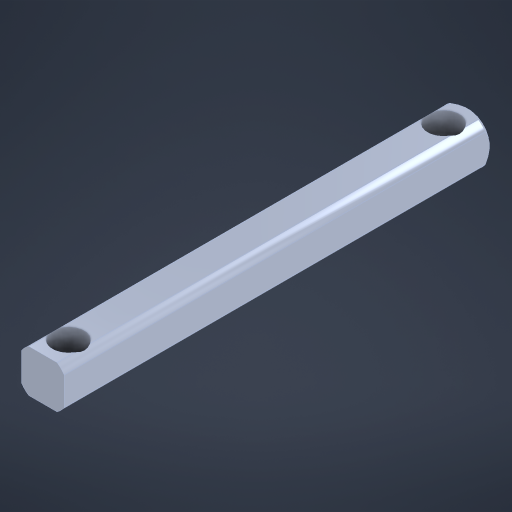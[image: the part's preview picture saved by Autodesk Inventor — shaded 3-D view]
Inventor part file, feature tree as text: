
AUTODESK INVENTOR PART (.ipt)
format: ipt  version: 2024 (Build 280153000, 153)  size: 311,808 bytes
history: native  units: in
note: dims shown in document units (in); Inventor stores cm internally (conversion verified against a paired STEP export)
features: other x50, sketch x3, extrude x2, thicken_offset x1, hole x1
ambient origin geometry x8: Origin, YZ Plane, XZ Plane, XY Plane, X Axis, Y Axis, Z Axis, Center Point
bodies: Solid1 (feature_tree)
feature tree (57):
  other  "Table"
  other  "Shaft HS 0.5 in"
  other  "Shaft HS 1.0 in"
  other  "Shaft HS 1.5 in"
  other  "Shaft HS 2.0 in"
  other  "Shaft HS 2.5 in"
  other  "Shaft HS 3.0 in"
  other  "Shaft HS 3.5 in"
  other  "Shaft HS 4.0 in"
  other  "Shaft HS 4.5 in"
  other  "Shaft HS 5.0 in"
  other  "Shaft HS 5.5 in"
  other  "Shaft HS 6.0 in"
  other  "Shaft HS 6.5 in"
  other  "Shaft HS 7.0 in"
  other  "Shaft HS 7.5 in"
  other  "Shaft HS 8.0 in"
  other  "Shaft HS 8.5 in"
  other  "Shaft HS 9.0 in"
  other  "Shaft HS 9.5 in"
  other  "Shaft HS 10.0 in"
  other  "Shaft HS 10.5 in"
  other  "Shaft HS 11.0 in"
  other  "Shaft HS 11.5 in"
  other  "Shaft HS 12.0 in"
  other  "Shaft HS 12.5 in"
  other  "Shaft HS 13.0 in"
  other  "Shaft HS 13.5 in"
  other  "Shaft HS 14.0 in"
  other  "Shaft HS 14.5 in"
  other  "Shaft HS 15.0 in"
  other  "Shaft HS 15.5 in"
  other  "Shaft HS 16.0 in"
  other  "Shaft HS 16.5 in"
  other  "Shaft HS 17.0 in"
  other  "Shaft HS 17.5 in"
  other  "Shaft HS 18.0 in"
  other  "Shaft HS 18.5 in"
  other  "Shaft HS 19.0 in"
  other  "Shaft HS 19.5 in"
  other  "Shaft HS 20.0 in"
  other  "Shaft HS 20.5 in"
  other  "Shaft HS 21.0 in"
  other  "Shaft HS 21.5 in"
  other  "Shaft HS 22.0 in"
  other  "Shaft HS 22.5 in"
  other  "Shaft HS 23.0 in"
  other  "Shaft HS 23.5 in"
  other  "Shaft HS 24.0 in"
  extrude  "Extrusion1"  Depth=12.1875in
  thicken_offset  "Thicken1"
  extrude  "Extrusion2"  Depth=21.625in
  hole  "Hole1"  [1 undecoded]
  sketch  "Sketch2"  dims[d0=0.0625in d1=0.0in d2=12.1875in]
  sketch  "Sketch3"  dims[d3=12.125in d4=21.625in]
  sketch  "Sketch6"  dims[d5=0.0in d9=0.15in d11=0.1875in d12=0.75in d13=0.375in d14=0.25in d15=0.5635in d16=1.0in d17=0.8108in d18=2.2in]
  other  "Cut-Revolve3"
note: 1 required parameter value undecoded (feature->parameter linkage not recoverable at this tier; creation-order binding heuristic only, values carry confidence <= 0.55)
